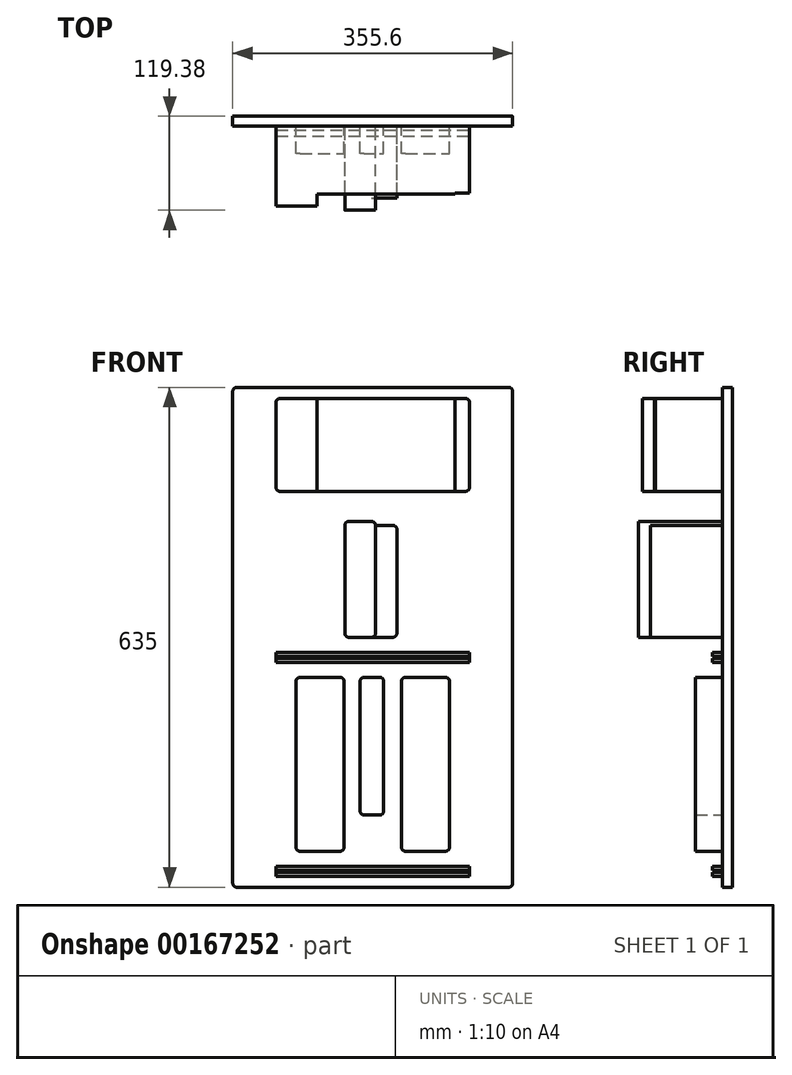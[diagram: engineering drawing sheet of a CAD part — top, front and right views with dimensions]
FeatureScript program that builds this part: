
annotation { "Feature Type Name" : "Feature", "Feature Type Description" : "" }
export const myFeature = defineFeature(function(context is Context, id is Id, definition is map)
    precondition{}
    {
        {
            var Q0;
            Q0=qCreatedBy(makeId("Front.planeOp"),FACE);
            var sketch = newSketch(context, id + "F0", { "sketchPlane" : qUnion([Q0])});
            skLineSegment(sketch, "E0.bottom", {"start": v(0, 0) * mm, "end": v(52.32, 0) * mm});
            skLineSegment(sketch, "E0.top", {"start": v(0, 118.11) * mm, "end": v(52.32, 118.11) * mm});
            skLineSegment(sketch, "E0.left", {"start": v(0, 0) * mm, "end": v(0, 118.11) * mm});
            skLineSegment(sketch, "E0.right", {"start": v(52.32, 0) * mm, "end": v(52.32, 118.1) * mm});
            skLineSegment(sketch, "E1.bottom", {"start": v(52.32, 118.11) * mm, "end": v(87.38, 118.11) * mm});
            skLineSegment(sketch, "E1.top", {"start": v(52.32, 0) * mm, "end": v(87.38, 0) * mm});
            skLineSegment(sketch, "E1.left", {"start": v(52.32, 118.1) * mm, "end": v(52.32, 0) * mm});
            skLineSegment(sketch, "E1.right", {"start": v(87.38, 118.1) * mm, "end": v(87.38, 0) * mm});
            skLineSegment(sketch, "E2.bottom", {"start": v(87.38, 0) * mm, "end": v(157.48, 0) * mm});
            skLineSegment(sketch, "E2.top", {"start": v(87.38, 118.11) * mm, "end": v(157.48, 118.11) * mm});
            skLineSegment(sketch, "E2.left", {"start": v(87.38, 0) * mm, "end": v(87.38, 118.1) * mm});
            skLineSegment(sketch, "E2.right", {"start": v(157.48, 0) * mm, "end": v(157.48, 118.1) * mm});
            skLineSegment(sketch, "E3.bottom", {"start": v(157.48, 0) * mm, "end": v(192.53, 0) * mm});
            skLineSegment(sketch, "E3.top", {"start": v(157.48, 118.11) * mm, "end": v(192.53, 118.11) * mm});
            skLineSegment(sketch, "E3.right", {"start": v(192.53, 0) * mm, "end": v(192.53, 118.1) * mm});
            skLineSegment(sketch, "E4.bottom", {"start": v(192.53, 118.11) * mm, "end": v(227.58, 118.11) * mm});
            skLineSegment(sketch, "E4.top", {"start": v(192.53, 0) * mm, "end": v(227.58, 0) * mm});
            skLineSegment(sketch, "E4.left", {"start": v(192.53, 118.1) * mm, "end": v(192.53, 0) * mm});
            skLineSegment(sketch, "E4.right", {"start": v(227.58, 118.1) * mm, "end": v(227.58, 0) * mm});
            skLineSegment(sketch, "E5.bottom", {"start": v(227.58, 0) * mm, "end": v(245.62, 0) * mm});
            skLineSegment(sketch, "E5.top", {"start": v(227.58, 118.11) * mm, "end": v(245.62, 118.11) * mm});
            skLineSegment(sketch, "E5.left", {"start": v(227.58, 0) * mm, "end": v(227.58, 118.1) * mm});
            skLineSegment(sketch, "E5.right", {"start": v(245.62, 0) * mm, "end": v(245.62, 118.11) * mm});
            skLineSegment(sketch, "E6.bottom", {"start": v(87.38, -38.1) * mm, "end": v(126.24, -38.1) * mm});
            skLineSegment(sketch, "E6.top", {"start": v(87.38, -185.42) * mm, "end": v(126.24, -185.42) * mm});
            skLineSegment(sketch, "E6.left", {"start": v(87.38, -38.1) * mm, "end": v(87.38, -185.42) * mm});
            skLineSegment(sketch, "E6.right", {"start": v(126.24, -38.1) * mm, "end": v(126.24, -185.42) * mm});
            skLineSegment(sketch, "E7.bottom", {"start": v(126.24, -185.42) * mm, "end": v(153.42, -185.42) * mm});
            skLineSegment(sketch, "E7.top", {"start": v(126.24, -43.18) * mm, "end": v(153.42, -43.18) * mm});
            skLineSegment(sketch, "E7.left", {"start": v(126.24, -185.42) * mm, "end": v(126.24, -43.18) * mm});
            skLineSegment(sketch, "E7.right", {"start": v(153.42, -185.42) * mm, "end": v(153.42, -43.18) * mm});
            skLineSegment(sketch, "E8.bottom", {"start": v(25.4, -236.22) * mm, "end": v(86.36, -236.22) * mm});
            skLineSegment(sketch, "E8.top", {"start": v(25.4, -457.2) * mm, "end": v(86.36, -457.2) * mm});
            skLineSegment(sketch, "E8.left", {"start": v(25.4, -236.22) * mm, "end": v(25.4, -457.2) * mm});
            skLineSegment(sketch, "E8.right", {"start": v(86.36, -236.22) * mm, "end": v(86.36, -457.2) * mm});
            skLineSegment(sketch, "E9.bottom", {"start": v(159.26, -236.22) * mm, "end": v(220.22, -236.22) * mm});
            skLineSegment(sketch, "E9.top", {"start": v(159.26, -457.2) * mm, "end": v(220.22, -457.2) * mm});
            skLineSegment(sketch, "E9.left", {"start": v(159.26, -236.22) * mm, "end": v(159.26, -457.2) * mm});
            skLineSegment(sketch, "E9.right", {"start": v(220.22, -236.22) * mm, "end": v(220.22, -457.2) * mm});
            skLineSegment(sketch, "E10.bottom", {"start": v(106.8, -236.22) * mm, "end": v(136.78, -236.22) * mm});
            skLineSegment(sketch, "E10.top", {"start": v(106.8, -411.23) * mm, "end": v(136.78, -411.23) * mm});
            skLineSegment(sketch, "E10.left", {"start": v(106.8, -236.22) * mm, "end": v(106.8, -411.23) * mm});
            skLineSegment(sketch, "E10.right", {"start": v(136.78, -236.22) * mm, "end": v(136.78, -411.23) * mm});
            skLineSegment(sketch, "E11.bottom", {"start": v(-105.8, 182.88) * mm, "end": v(351.4, 182.88) * mm, "construction": true});
            skLineSegment(sketch, "E11.top", {"start": v(-105.8, -553.72) * mm, "end": v(351.4, -553.72) * mm, "construction": true});
            skLineSegment(sketch, "E11.left", {"start": v(-105.8, 182.88) * mm, "end": v(-105.8, -553.72) * mm, "construction": true});
            skLineSegment(sketch, "E11.right", {"start": v(351.4, 182.88) * mm, "end": v(351.4, -553.72) * mm, "construction": true});
            skSolve(sketch);
        }
        {
            var Q0;
            Q0=makeQuery(id+"F0.imprint","IMPRINT",FACE,{"disambiguationData":[TD([[makeQuery(id+"F0.imprint","IMPRINT",EDGE,{"derivedFrom":sQuery(id+"F0.wireOp",EDGE,"E5.bottom")}),1.0]])]});
            extrude(context, id + "F1", {"entities" : qUnion([Q0]), "depth" : 85.1 * mm});
        }
        {
            var Q0;
            Q0=makeQuery(id+"F0.imprint","IMPRINT",FACE,{"disambiguationData":[TD([[makeQuery(id+"F0.imprint","IMPRINT",EDGE,{"derivedFrom":sQuery(id+"F0.wireOp",EDGE,"E4.bottom")}),-1.0]])]});
            var Q1;
            Q1=makeQuery(id+"F0.imprint","IMPRINT",FACE,{"disambiguationData":[TD([[makeQuery(id+"F0.imprint","IMPRINT",EDGE,{"derivedFrom":sQuery(id+"F0.wireOp",EDGE,"E3.bottom")}),1.0]])]});
            var Q2;
            Q2=makeQuery(id+"F0.imprint","IMPRINT",FACE,{"disambiguationData":[TD([[makeQuery(id+"F0.imprint","IMPRINT",EDGE,{"derivedFrom":sQuery(id+"F0.wireOp",EDGE,"E2.bottom")}),1.0]])]});
            var Q3;
            Q3=makeQuery(id+"F0.imprint","IMPRINT",FACE,{"disambiguationData":[TD([[makeQuery(id+"F0.imprint","IMPRINT",EDGE,{"derivedFrom":sQuery(id+"F0.wireOp",EDGE,"E1.bottom")}),-1.0]])]});
            extrude(context, id + "F2", {"entities" : qUnion([Q0, Q1, Q2, Q3]), "operationType" : NewBodyOperationType.ADD, "depth" : 86.36 * mm});
        }
        {
            var Q0;
            Q0=makeQuery(id+"F0.imprint","IMPRINT",FACE,{"disambiguationData":[TD([[makeQuery(id+"F0.imprint","IMPRINT",EDGE,{"derivedFrom":sQuery(id+"F0.wireOp",EDGE,"E0.bottom")}),1.0]])]});
            extrude(context, id + "F3", {"entities" : qUnion([Q0]), "operationType" : NewBodyOperationType.ADD, "depth" : 101.6 * mm});
        }
        {
            var Q0;
            Q0=makeQuery(id+"F0.imprint","IMPRINT",FACE,{"disambiguationData":[TD([[makeQuery(id+"F0.imprint","IMPRINT",EDGE,{"derivedFrom":sQuery(id+"F0.wireOp",EDGE,"E7.bottom")}),1.0]])]});
            extrude(context, id + "F4", {"entities" : qUnion([Q0]), "depth" : 91.44 * mm});
        }
        {
            var Q0;
            Q0=makeQuery(id+"F0.imprint","IMPRINT",FACE,{"disambiguationData":[TD([[makeQuery(id+"F0.imprint","IMPRINT",EDGE,{"derivedFrom":sQuery(id+"F0.wireOp",EDGE,"E6.bottom")}),-1.0]])]});
            extrude(context, id + "F5", {"entities" : qUnion([Q0]), "operationType" : NewBodyOperationType.ADD, "depth" : 106.68 * mm});
        }
        {
            var Q0;
            Q0=makeQuery(id+"F0.imprint","IMPRINT",FACE,{"disambiguationData":[TD([[makeQuery(id+"F0.imprint","IMPRINT",EDGE,{"derivedFrom":sQuery(id+"F0.wireOp",EDGE,"E8.bottom")}),-1.0]])]});
            var Q1;
            Q1=makeQuery(id+"F0.imprint","IMPRINT",FACE,{"disambiguationData":[TD([[makeQuery(id+"F0.imprint","IMPRINT",EDGE,{"derivedFrom":sQuery(id+"F0.wireOp",EDGE,"E9.bottom")}),-1.0]])]});
            var Q2;
            Q2=makeQuery(id+"F0.imprint","IMPRINT",FACE,{"disambiguationData":[TD([[makeQuery(id+"F0.imprint","IMPRINT",EDGE,{"derivedFrom":sQuery(id+"F0.wireOp",EDGE,"E10.bottom")}),-1.0]])]});
            extrude(context, id + "F6", {"entities" : qUnion([Q0, Q1, Q2]), "depth" : 34.54 * mm});
        }
        {
            var Q0;
            Q0=qCreatedBy(makeId("Front.planeOp"),FACE);
            var sketch = newSketch(context, id + "F7", { "sketchPlane" : qUnion([Q0])});
            skLineSegment(sketch, "E12.bottom", {"start": v(0, -204.47) * mm, "end": v(245.62, -204.47) * mm});
            skLineSegment(sketch, "E12.top", {"start": v(0, -209.55) * mm, "end": v(245.62, -209.55) * mm});
            skLineSegment(sketch, "E12.left", {"start": v(0, -204.47) * mm, "end": v(0, -209.55) * mm});
            skLineSegment(sketch, "E12.right", {"start": v(245.62, -204.47) * mm, "end": v(245.62, -209.55) * mm});
            skLineSegment(sketch, "E13.top", {"start": v(0, -212.1) * mm, "end": v(245.62, -212.1) * mm});
            skLineSegment(sketch, "E13.left", {"start": v(0, -209.55) * mm, "end": v(0, -212.1) * mm});
            skLineSegment(sketch, "E13.right", {"start": v(245.62, -209.55) * mm, "end": v(245.62, -212.1) * mm});
            skLineSegment(sketch, "E14.top", {"start": v(0, -217.17) * mm, "end": v(245.62, -217.17) * mm});
            skLineSegment(sketch, "E14.left", {"start": v(0, -212.1) * mm, "end": v(0, -217.17) * mm});
            skLineSegment(sketch, "E14.right", {"start": v(245.62, -212.1) * mm, "end": v(245.62, -217.17) * mm});
            skLineSegment(sketch, "E15.bottom", {"start": v(0, -476.25) * mm, "end": v(245.62, -476.25) * mm});
            skLineSegment(sketch, "E15.top", {"start": v(0, -481.33) * mm, "end": v(245.62, -481.33) * mm});
            skLineSegment(sketch, "E15.left", {"start": v(0, -476.25) * mm, "end": v(0, -481.33) * mm});
            skLineSegment(sketch, "E15.right", {"start": v(245.62, -476.25) * mm, "end": v(245.62, -481.33) * mm});
            skLineSegment(sketch, "E16.top", {"start": v(0, -483.87) * mm, "end": v(245.62, -483.87) * mm});
            skLineSegment(sketch, "E16.left", {"start": v(0, -481.33) * mm, "end": v(0, -483.87) * mm});
            skLineSegment(sketch, "E16.right", {"start": v(245.62, -481.33) * mm, "end": v(245.62, -483.87) * mm});
            skLineSegment(sketch, "E17.top", {"start": v(0, -488.95) * mm, "end": v(245.62, -488.95) * mm});
            skLineSegment(sketch, "E17.left", {"start": v(0, -483.87) * mm, "end": v(0, -488.95) * mm});
            skLineSegment(sketch, "E17.right", {"start": v(245.62, -483.87) * mm, "end": v(245.62, -488.95) * mm});
            skSolve(sketch);
        }
        {
            var Q0;
            Q0=makeQuery(id+"F7.imprint","IMPRINT",FACE,{"disambiguationData":[TD([[makeQuery(id+"F7.imprint","IMPRINT",EDGE,{"derivedFrom":sQuery(id+"F7.wireOp",EDGE,"E12.bottom")}),-1.0]])]});
            var Q1;
            Q1=makeQuery(id+"F7.imprint","IMPRINT",FACE,{"disambiguationData":[TD([[makeQuery(id+"F7.imprint","IMPRINT",EDGE,{"derivedFrom":sQuery(id+"F7.wireOp",EDGE,"E13.top")}),-1.0]])]});
            var Q2;
            Q2=makeQuery(id+"F7.imprint","IMPRINT",FACE,{"disambiguationData":[TD([[makeQuery(id+"F7.imprint","IMPRINT",EDGE,{"derivedFrom":sQuery(id+"F7.wireOp",EDGE,"E16.top")}),-1.0]])]});
            var Q3;
            Q3=makeQuery(id+"F7.imprint","IMPRINT",FACE,{"disambiguationData":[TD([[makeQuery(id+"F7.imprint","IMPRINT",EDGE,{"derivedFrom":sQuery(id+"F7.wireOp",EDGE,"E15.bottom")}),-1.0]])]});
            extrude(context, id + "F8", {"entities" : qUnion([Q0, Q1, Q2, Q3]), "depth" : 12.7 * mm});
        }
        {
            var Q0;
            Q0=makeQuery(id+"F7.imprint","IMPRINT",FACE,{"disambiguationData":[TD([[makeQuery(id+"F7.imprint","IMPRINT",EDGE,{"derivedFrom":sQuery(id+"F7.wireOp",EDGE,"E12.top")}),-1.0]])]});
            var Q1;
            Q1=makeQuery(id+"F7.imprint","IMPRINT",FACE,{"disambiguationData":[TD([[makeQuery(id+"F7.imprint","IMPRINT",EDGE,{"derivedFrom":sQuery(id+"F7.wireOp",EDGE,"E15.top")}),-1.0]])]});
            extrude(context, id + "F9", {"entities" : qUnion([Q0, Q1]), "depth" : 5.08 * mm});
        }
        {
            var Q0;
            Q0=qCreatedBy(makeId("Front.planeOp"),FACE);
            var sketch = newSketch(context, id + "F10", { "sketchPlane" : qUnion([Q0])});
            skLineSegment(sketch, "E18.bottom", {"start": v(-55, 132.08) * mm, "end": v(300.6, 132.08) * mm});
            skLineSegment(sketch, "E18.top", {"start": v(-55, -502.92) * mm, "end": v(300.6, -502.92) * mm});
            skLineSegment(sketch, "E18.left", {"start": v(-55, 132.08) * mm, "end": v(-55, -502.92) * mm});
            skLineSegment(sketch, "E18.right", {"start": v(300.6, 132.08) * mm, "end": v(300.6, -502.92) * mm});
            skSolve(sketch);
        }
        {
            var Q0;
            Q0 = qSketchRegion(id + "F10", true);
            extrude(context, id + "F11", {"entities" : qUnion([Q0]), "oppositeDirection" : true, "depth" : 12.7 * mm});
        }
        {
            var Q0;
            Q0=makeQuery(id+"F6.opExtrude","SWEPT_EDGE",EDGE,{"disambiguationData":[OSD([sQuery(id+"F0.wireOp",EDGE,"E8.bottom"),sQuery(id+"F0.wireOp",EDGE,"E8.right")])]});
            var Q1;
            Q1=makeQuery(id+"F6.opExtrude","SWEPT_EDGE",EDGE,{"disambiguationData":[OSD([sQuery(id+"F0.wireOp",EDGE,"E10.bottom"),sQuery(id+"F0.wireOp",EDGE,"E10.right")])]});
            var Q2;
            Q2=makeQuery(id+"F6.opExtrude","SWEPT_EDGE",EDGE,{"disambiguationData":[OSD([sQuery(id+"F0.wireOp",EDGE,"E9.bottom"),sQuery(id+"F0.wireOp",EDGE,"E9.right")])]});
            var Q3;
            Q3=makeQuery(id+"F6.opExtrude","SWEPT_EDGE",EDGE,{"disambiguationData":[OSD([sQuery(id+"F0.wireOp",EDGE,"E9.bottom"),sQuery(id+"F0.wireOp",EDGE,"E9.left")])]});
            var Q4;
            Q4=makeQuery(id+"F6.opExtrude","SWEPT_EDGE",EDGE,{"disambiguationData":[OSD([sQuery(id+"F0.wireOp",EDGE,"E8.bottom"),sQuery(id+"F0.wireOp",EDGE,"E8.left")])]});
            var Q5;
            Q5=makeQuery(id+"F6.opExtrude","SWEPT_EDGE",EDGE,{"disambiguationData":[OSD([sQuery(id+"F0.wireOp",EDGE,"E8.top"),sQuery(id+"F0.wireOp",EDGE,"E8.left")])]});
            var Q6;
            Q6=makeQuery(id+"F6.opExtrude","SWEPT_EDGE",EDGE,{"disambiguationData":[OSD([sQuery(id+"F0.wireOp",EDGE,"E10.top"),sQuery(id+"F0.wireOp",EDGE,"E10.left")])]});
            var Q7;
            Q7=makeQuery(id+"F6.opExtrude","SWEPT_EDGE",EDGE,{"disambiguationData":[OSD([sQuery(id+"F0.wireOp",EDGE,"E9.top"),sQuery(id+"F0.wireOp",EDGE,"E9.left")])]});
            var Q8;
            Q8=makeQuery(id+"F6.opExtrude","SWEPT_EDGE",EDGE,{"disambiguationData":[OSD([sQuery(id+"F0.wireOp",EDGE,"E8.top"),sQuery(id+"F0.wireOp",EDGE,"E8.right")])]});
            var Q9;
            Q9=makeQuery(id+"F6.opExtrude","SWEPT_EDGE",EDGE,{"disambiguationData":[OSD([sQuery(id+"F0.wireOp",EDGE,"E10.top"),sQuery(id+"F0.wireOp",EDGE,"E10.right")])]});
            var Q10;
            Q10=makeQuery(id+"F6.opExtrude","SWEPT_EDGE",EDGE,{"disambiguationData":[OSD([sQuery(id+"F0.wireOp",EDGE,"E9.top"),sQuery(id+"F0.wireOp",EDGE,"E9.right")])]});
            fillet(context, id + "F12", {"entities" : qUnion([Q0, Q1, Q2, Q3, Q4, Q5, Q6, Q7, Q8, Q9, Q10]), "radius" : 5.08 * mm, "tangentPropagation" : true, "allowEdgeOverflow" : false});
        }
        {
            var Q0;
            Q0=makeQuery(id+"F6.opExtrude","SWEPT_EDGE",EDGE,{"disambiguationData":[OSD([sQuery(id+"F0.wireOp",EDGE,"E10.bottom"),sQuery(id+"F0.wireOp",EDGE,"E10.left")])]});
            var Q1;
            Q1=makeQuery(id+"F5.opExtrude","SWEPT_EDGE",EDGE,{"disambiguationData":[OSD([sQuery(id+"F0.wireOp",EDGE,"E6.top"),sQuery(id+"F0.wireOp",EDGE,"E6.left")])]});
            var Q2;
            Q2=makeQuery(id+"F5.opExtrude","SWEPT_EDGE",EDGE,{"disambiguationData":[OSD([sQuery(id+"F0.wireOp",EDGE,"E6.bottom"),sQuery(id+"F0.wireOp",EDGE,"E6.left")])]});
            var Q3;
            Q3=makeQuery(id+"F4.opExtrude","SWEPT_EDGE",EDGE,{"disambiguationData":[OSD([sQuery(id+"F0.wireOp",EDGE,"E7.top"),sQuery(id+"F0.wireOp",EDGE,"E7.right")])]});
            var Q4;
            Q4=makeQuery(id+"F5.opExtrude","SWEPT_EDGE",EDGE,{"disambiguationData":[OSD([sQuery(id+"F0.wireOp",EDGE,"E6.bottom"),sQuery(id+"F0.wireOp",EDGE,"E6.right")])]});
            var Q5;
            Q5=makeQuery(id+"F4.opExtrude","SWEPT_EDGE",EDGE,{"disambiguationData":[OSD([sQuery(id+"F0.wireOp",EDGE,"E7.bottom"),sQuery(id+"F0.wireOp",EDGE,"E7.right")])]});
            var Q6;
            Q6=makeQuery(id+"F5.opExtrude","SWEPT_EDGE",EDGE,{"disambiguationData":[OSD([sQuery(id+"F0.wireOp",EDGE,"E6.top"),sQuery(id+"F0.wireOp",EDGE,"E7.bottom"),sQuery(id+"F0.wireOp",EDGE,"E7.left")])]});
            fillet(context, id + "F13", {"entities" : qUnion([Q0, Q1, Q2, Q3, Q4, Q5, Q6]), "radius" : 5.08 * mm, "tangentPropagation" : true, "allowEdgeOverflow" : false});
        }
        {
            var Q0;
            Q0=makeQuery(id+"F3.opExtrude","SWEPT_EDGE",EDGE,{"disambiguationData":[OSD([sQuery(id+"F0.wireOp",EDGE,"E0.top"),sQuery(id+"F0.wireOp",EDGE,"E0.left")])]});
            var Q1;
            Q1=makeQuery(id+"F3.opExtrude","SWEPT_EDGE",EDGE,{"disambiguationData":[OSD([sQuery(id+"F0.wireOp",EDGE,"E0.bottom"),sQuery(id+"F0.wireOp",EDGE,"E0.left")])]});
            var Q2;
            Q2=makeQuery(id+"F1.opExtrude","SWEPT_EDGE",EDGE,{"disambiguationData":[OSD([sQuery(id+"F0.wireOp",EDGE,"E5.top"),sQuery(id+"F0.wireOp",EDGE,"E5.right")])]});
            var Q3;
            Q3=makeQuery(id+"F1.opExtrude","SWEPT_EDGE",EDGE,{"disambiguationData":[OSD([sQuery(id+"F0.wireOp",EDGE,"E5.bottom"),sQuery(id+"F0.wireOp",EDGE,"E5.right")])]});
            fillet(context, id + "F14", {"entities" : qUnion([Q0, Q1, Q2, Q3]), "radius" : 5.08 * mm, "tangentPropagation" : true, "allowEdgeOverflow" : false});
        }
        {
            var Q0;
            Q0=makeQuery(id+"F11.opExtrude","SWEPT_EDGE",EDGE,{"disambiguationData":[OSD([sQuery(id+"F10.wireOp",EDGE,"E18.bottom"),sQuery(id+"F10.wireOp",EDGE,"E18.left")])]});
            var Q1;
            Q1=makeQuery(id+"F11.opExtrude","SWEPT_EDGE",EDGE,{"disambiguationData":[OSD([sQuery(id+"F10.wireOp",EDGE,"E18.bottom"),sQuery(id+"F10.wireOp",EDGE,"E18.right")])]});
            var Q2;
            Q2=makeQuery(id+"F11.opExtrude","SWEPT_EDGE",EDGE,{"disambiguationData":[OSD([sQuery(id+"F10.wireOp",EDGE,"E18.top"),sQuery(id+"F10.wireOp",EDGE,"E18.right")])]});
            var Q3;
            Q3=makeQuery(id+"F11.opExtrude","SWEPT_EDGE",EDGE,{"disambiguationData":[OSD([sQuery(id+"F10.wireOp",EDGE,"E18.top"),sQuery(id+"F10.wireOp",EDGE,"E18.left")])]});
            fillet(context, id + "F15", {"entities" : qUnion([Q0, Q1, Q2, Q3]), "radius" : 5.08 * mm, "tangentPropagation" : true, "allowEdgeOverflow" : false});
        }
    });
